# Revit family: MD2xx-4200-48
name_source: partatom
category: Lighting Fixtures
units: mm (PartAtom-declared; Revit-internal decimal feet)

## family parameters
Always vertical = Yes
Cut with Voids When Loaded = No
Host = Ceiling
Light Source = Yes
OmniClass Number = 23.80.70.11.14.17
OmniClass Title = Direct/Indirect
Part Type = Normal
Room Calculation Point = No
Round Connector Dimension = Use Diameter
Shared = No

## types (6) — shared parameters
Color Filter = 16777215
Description = LED-Recessed Medical Patient Ambient/Exam Luminaire
Diffuser Finish = Acrylic - Viscor - Frosted Round
Dimming Lamp Color Temperature Shift = <None>
Emit Shape Visible in Rendering = No
Emit from Rectangle Length = 3' - 11 3/4"
Emit from Rectangle Width = 0' - 7 3/4"
Housing Finish = Metal - Viscor - White
Lamp = LED
Length = 3' - 11 3/4"
Lens Finish = Acrylic - Viscor - Flat Frosted Prismatic P12
Manufacturer = Certolux By Viscor
Model = MD2-4200
Tilt Angle = 90.00°
URL = https://www.viscor.com
Voltage = 120 V
Width = 0' - 7 3/4"

## per-type parameters (varying)
| type | Apparent Load | Lamp Wattage | Photometric Web File |
| MD2xx-4200-48-LED840K052LUNV (Exam On) | 25 VA | 25 VA | MD2IG-4200-48-LED840K52Lxxx (EXAM ON).IES |
| MD2xx-4200-48-LED840K052LUNV (Ambient On) | 25 VA | 25 VA | MD2IG-4200-48-LED840K52Lxxx (AMBIENT ON).IES |
| MD2xx-4200-48-LED840K052LUNV (All On) | 50 VA | 50 VA | MD2IG-4200-48-LED840K52Lxxx (ALL ON).IES |
| MD2xx-4200-48-LED840K026LUNV (Exam On) | 13 VA | 13 VA | MD2IG-4200-48-LED840K26Lxxx (EXAM ON).ies |
| MD2xx-4200-48-LED840K026LUNV (Ambient On) | 13 VA | 13 VA | MD2IG-4200-48-LED840K26Lxxx(AMBIENT ON).ies |
| MD2xx-4200-48-LED840K026LUNV (All On) | 25 VA | 25 VA | MD2IG-4200-48-LED840K26Lxxx(All ON).ies |

## geometry (parser evidence)
native form markers: Sweep x3
no freeform markers — native parametric forms only
